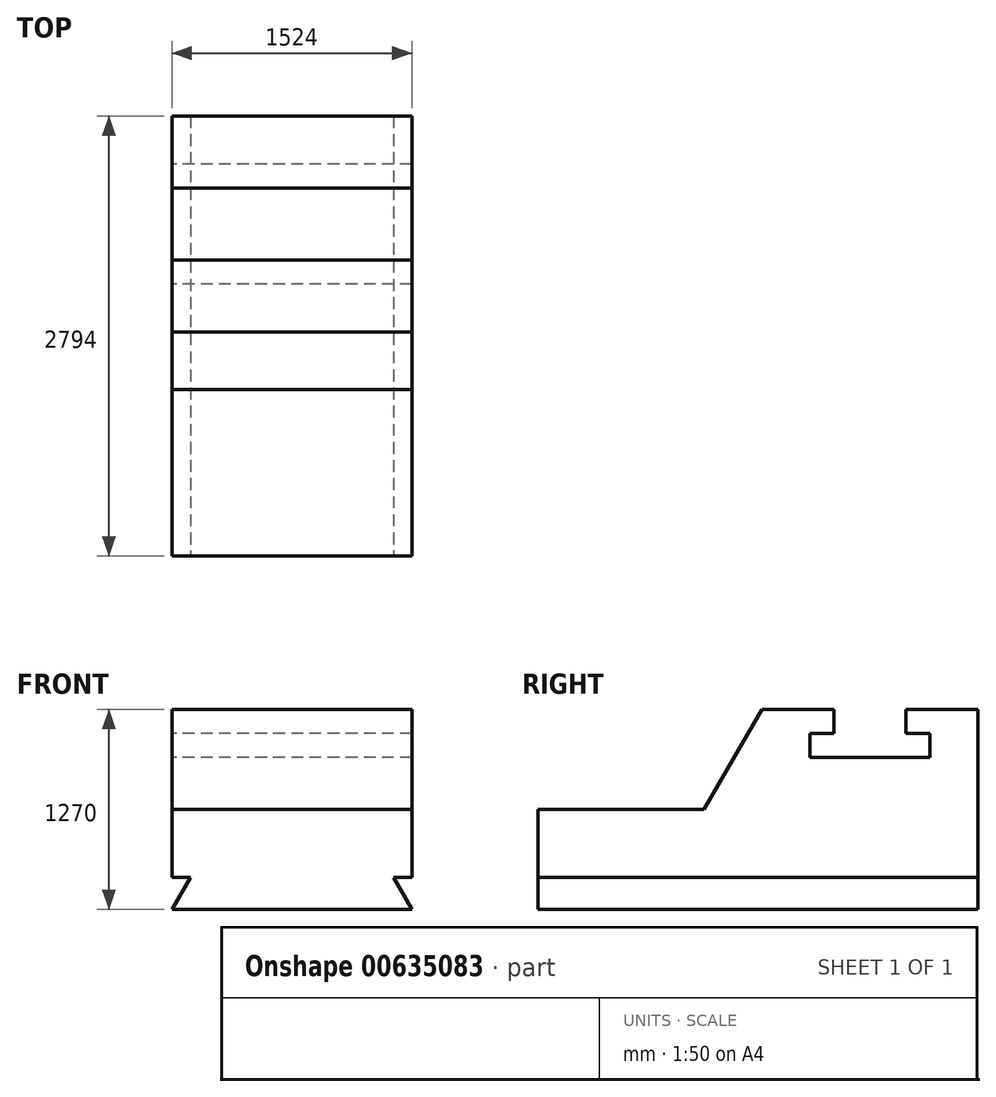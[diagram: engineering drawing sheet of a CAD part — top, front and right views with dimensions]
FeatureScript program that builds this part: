
annotation { "Feature Type Name" : "Feature", "Feature Type Description" : "" }
export const myFeature = defineFeature(function(context is Context, id is Id, definition is map)
    precondition{}
    {
        {
            var Q0;
            Q0=qCreatedBy(makeId("Right.planeOp"),FACE);
            var sketch = newSketch(context, id + "F0", { "sketchPlane" : qUnion([Q0])});
            skLineSegment(sketch, "E0", {"start": v(-473.4, -83.02) * mm, "end": v(2320.6, -83.02) * mm});
            skLineSegment(sketch, "E1", {"start": v(2320.6, -83.02) * mm, "end": v(2320.6, 1186.98) * mm});
            skLineSegment(sketch, "E2", {"start": v(2320.6, 1186.98) * mm, "end": v(1863.4, 1186.98) * mm});
            skLineSegment(sketch, "E3", {"start": v(-473.4, -83.02) * mm, "end": v(-473.4, 551.98) * mm});
            skLineSegment(sketch, "E4", {"start": v(-473.4, 551.98) * mm, "end": v(582.39, 551.98) * mm});
            skLineSegment(sketch, "E5", {"start": v(949, 1186.98) * mm, "end": v(582.39, 551.98) * mm});
            skLineSegment(sketch, "E6", {"start": v(949, 1186.98) * mm, "end": v(1406.2, 1186.98) * mm});
            skLineSegment(sketch, "E7", {"start": v(1406.2, 1186.98) * mm, "end": v(1406.2, 1034.58) * mm});
            skLineSegment(sketch, "E8", {"start": v(1863.4, 1186.98) * mm, "end": v(1863.4, 1034.58) * mm});
            skLineSegment(sketch, "E9", {"start": v(2015.8, 882.18) * mm, "end": v(2015.8, 1034.58) * mm});
            skLineSegment(sketch, "E10", {"start": v(2015.8, 1034.58) * mm, "end": v(1863.4, 1034.58) * mm});
            skLineSegment(sketch, "E11", {"start": v(2015.8, 882.18) * mm, "end": v(1253.8, 882.18) * mm});
            skLineSegment(sketch, "E12", {"start": v(1253.8, 882.18) * mm, "end": v(1253.8, 1034.58) * mm});
            skLineSegment(sketch, "E13", {"start": v(1253.8, 1034.58) * mm, "end": v(1406.2, 1034.58) * mm});
            skLineSegment(sketch, "E14.trimOffspring", {"start": v(1406.2, 1186.98) * mm, "end": v(949, 1186.98) * mm});
            skSolve(sketch);
        }
        {
            var Q0;
            Q0 = qSketchRegion(id + "F0", true);
            extrude(context, id + "F1", {"entities" : qUnion([Q0]), "depth" : 1524 * mm, "offsetDistance" : 25.4 * mm});
        }
        {
            var Q0;
            Q0=makeQuery(id+"F1.opExtrude","SWEPT_FACE",FACE,{"disambiguationData":[OSD([sQuery(id+"F0.wireOp",EDGE,"E3")])]});
            var sketch = newSketch(context, id + "F2", { "sketchPlane" : qUnion([Q0])});
            skLineSegment(sketch, "E15", {"start": v(1524, -83.02) * mm, "end": v(1406.68, 120.18) * mm});
            skLineSegment(sketch, "E16", {"start": v(1524, -83.02) * mm, "end": v(1524, 120.18) * mm});
            skLineSegment(sketch, "E17", {"start": v(1524, 120.18) * mm, "end": v(1406.68, 120.18) * mm});
            skLineSegment(sketch, "E18", {"start": v(0, -83.02) * mm, "end": v(117.32, 120.18) * mm});
            skLineSegment(sketch, "E19", {"start": v(0, -83.02) * mm, "end": v(0, 120.18) * mm});
            skPoint(sketch, "E19.endSnap0", {"position": v(117.32, 120.18) * mm});
            skLineSegment(sketch, "E20", {"start": v(0, 120.18) * mm, "end": v(117.32, 120.18) * mm});
            skSolve(sketch);
        }
        {
            var Q0;
            Q0=makeQuery(id+"F2.imprint","IMPRINT",FACE,{"disambiguationData":[TD([[makeQuery(id+"F2.imprint","IMPRINT",EDGE,{"derivedFrom":sQuery(id+"F2.wireOp",EDGE,"E18")}),1.0]])]});
            var Q1;
            Q1=makeQuery(id+"F2.imprint","IMPRINT",FACE,{"disambiguationData":[TD([[makeQuery(id+"F2.imprint","IMPRINT",EDGE,{"derivedFrom":sQuery(id+"F2.wireOp",EDGE,"E15")}),-1.0]])]});
            extrude(context, id + "F3", {"entities" : qUnion([Q0, Q1]), "operationType" : NewBodyOperationType.REMOVE, "oppositeDirection" : true, "depth" : 2794 * mm, "offsetDistance" : 25.4 * mm});
        }
    });
